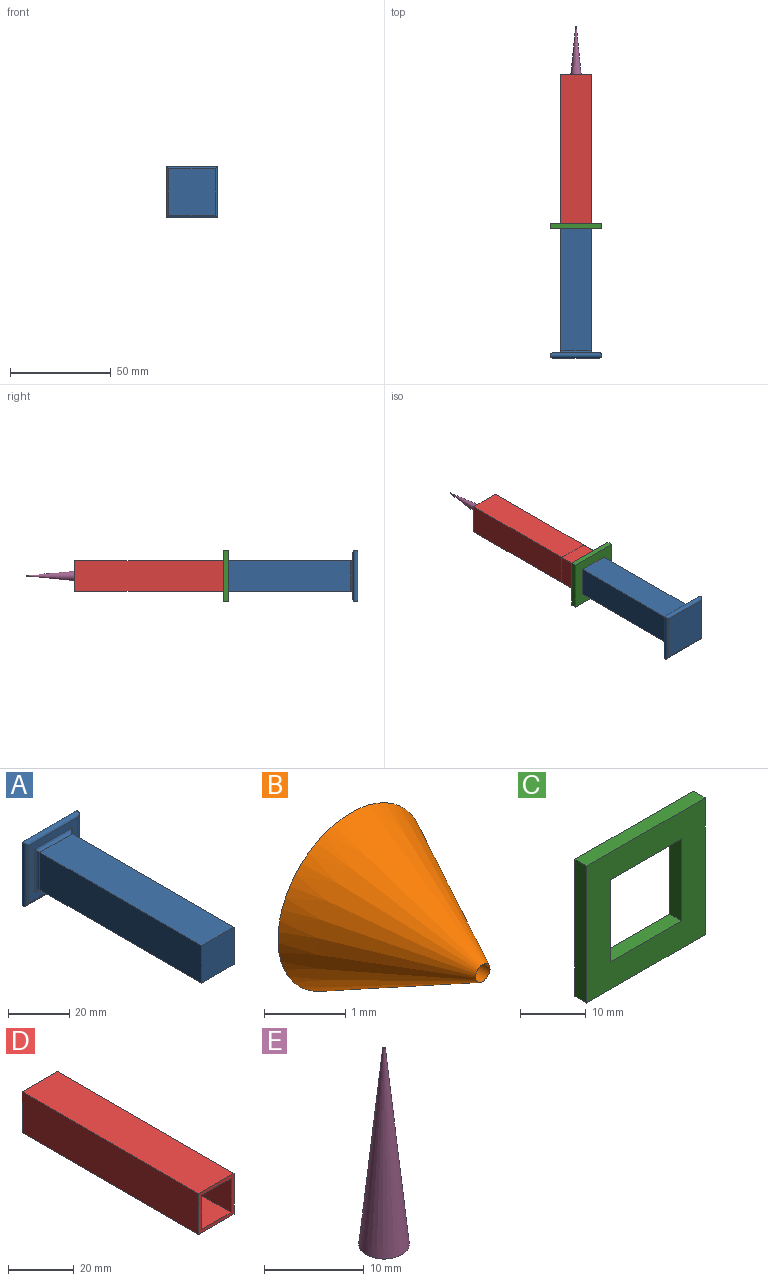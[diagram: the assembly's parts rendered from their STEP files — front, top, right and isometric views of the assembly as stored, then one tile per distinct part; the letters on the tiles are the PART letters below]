
ASSEMBLY  parts=5 mates=6
PART A: 15 faces, bbox 25.4x78.7x25.4 mm
  f0: plane 22.86x22.86mm, normal (0,-1,0), area 215.4mm2, adj f7,f8,f9,f10,f11,f12,f13,f14
  f1: plane 22.86x22.86mm, normal (0,1,0), area 522.6mm2, adj f11,f12,f13,f14
  f2: plane 74.93x14.99mm, normal (-1,0,0), area 1122.9mm2, adj f3,f5,f6,f7
  f3: plane 74.93x14.99mm, normal (0,0,-1), area 1122.9mm2, adj f2,f4,f6,f9
  f4: plane 74.93x14.99mm, normal (1,0,0), area 1122.9mm2, adj f3,f5,f6,f10
  f5: plane 74.93x14.99mm, normal (0,0,1), area 1122.9mm2, adj f2,f4,f6,f8
  f6: plane 14.99x14.99mm, normal (0,-1,0), area 224.6mm2, adj f2,f3,f4,f5
  f7: cylinder r=1.27mm len=17.53mm, axis (0,0,-1), area 31.7mm2, adj f0,f2,f8,f9
  f8: cylinder r=1.27mm len=17.53mm, axis (-1,0,0), area 31.7mm2, adj f0,f5,f7,f10
  f9: cylinder r=1.27mm len=17.53mm, axis (1,0,0), area 31.7mm2, adj f0,f3,f7,f10
  f10: cylinder r=1.27mm len=17.53mm, axis (0,0,1), area 31.7mm2, adj f0,f4,f8,f9
  f11: cylinder r=1.27mm len=25.41mm, axis (0,0,1), area 97.7mm2, adj f0,f1,f12,f13
  f12: cylinder r=1.27mm len=25.41mm, axis (1,0,0), area 97.7mm2, adj f0,f1,f11,f14
  f13: cylinder r=1.27mm len=25.41mm, axis (-1,0,0), area 97.7mm2, adj f0,f1,f11,f14
  f14: cylinder r=1.27mm len=25.41mm, axis (0,0,-1), area 97.7mm2, adj f0,f1,f12,f13
PART B: 3 faces, bbox 2.5x2.3x2.5 mm
  f0: plane 2.54x2.54mm, normal (0,1,0), area 5mm2, adj f1,f2
  f1: cone r=1.27mm half-angle=26.6deg, axis (0,1,0), area 11.2mm2, adj f0,f2
  f2: cylinder r=0.13mm len=2.29mm, axis (0,1,0), area 1.8mm2, adj f0,f1
PART C: 10 faces, bbox 25.4x2.5x25.4 mm
  f0: plane 25.4x2.54mm, normal (-1,0,0), area 64.5mm2, adj f1,f3,f4,f5
  f1: plane 25.4x2.54mm, normal (0,0,-1), area 64.5mm2, adj f0,f2,f4,f5
  f2: plane 25.4x2.54mm, normal (1,0,0), area 64.5mm2, adj f1,f3,f4,f5
  f3: plane 25.4x2.54mm, normal (0,0,1), area 64.5mm2, adj f0,f2,f4,f5
  f4: plane 25.4x25.4mm, normal (0,-1,0), area 412.9mm2, adj f0,f1,f2,f3,f6,f7,f8,f9
  f5: plane 25.4x25.4mm, normal (0,1,0), area 412.9mm2, adj f0,f1,f2,f3,f6,f7,f8,f9
  f6: plane 15.24x2.54mm, normal (1,0,0), area 38.7mm2, adj f4,f5,f7,f9
  f7: plane 15.24x2.54mm, normal (0,0,1), area 38.7mm2, adj f4,f5,f6,f8
  f8: plane 15.24x2.54mm, normal (-1,0,0), area 38.7mm2, adj f4,f5,f7,f9
  f9: plane 15.24x2.54mm, normal (0,0,-1), area 38.7mm2, adj f4,f5,f6,f8
PART D: 12 faces, bbox 15.2x76.2x15.2 mm
  f0: plane 76.2x15.24mm, normal (0,0,1), area 1161.3mm2, adj f1,f3,f4,f5
  f1: plane 76.2x15.24mm, normal (-1,0,0), area 1161.3mm2, adj f0,f2,f4,f5
  f2: plane 76.2x15.24mm, normal (0,0,-1), area 1161.3mm2, adj f1,f3,f4,f5
  f3: plane 76.2x15.24mm, normal (1,0,0), area 1161.3mm2, adj f0,f2,f4,f5
  f4: plane 15.24x15.24mm, normal (0,-1,0), area 71mm2, adj f0,f1,f2,f3,f6,f7,f8,f9
  f5: plane 15.24x15.24mm, normal (0,1,0), area 232.2mm2, adj f0,f1,f2,f3,f11
  f6: plane 73.66x12.7mm, normal (1,0,0), area 935.5mm2, adj f4,f7,f9,f10
  f7: plane 73.66x12.7mm, normal (0,0,1), area 935.5mm2, adj f4,f6,f8,f10
  f8: plane 73.66x12.7mm, normal (-1,0,0), area 935.5mm2, adj f4,f7,f9,f10
  f9: plane 73.66x12.7mm, normal (0,0,-1), area 935.5mm2, adj f4,f6,f8,f10
  f10: plane 12.7x12.7mm, normal (0,-1,0), area 161.2mm2, adj f6,f7,f8,f9,f11
  f11: cylinder r=0.13mm len=2.54mm, axis (0,1,0), area 2mm2, adj f5,f10
PART E: 3 faces, bbox 5.1x5.1x24.1 mm
  f0: plane 5.08x5.08mm, normal (0,0,-1), area 20.2mm2, adj f1,f2
  f1: cone r=2.54mm half-angle=5.7deg, axis (0,0,-1), area 203.2mm2, adj f0,f2
  f2: cylinder r=0.13mm len=24.13mm, axis (0,0,-1), area 19.3mm2, adj f0,f1
PLACE A rot(axis=(0.71,0,0.71),180deg) t=(-22.07,-49.11,36.07)mm
PLACE B t=(-22.07,88.68,36.07)mm
PLACE C t=(-22.07,17.56,36.07)mm
PLACE D t=(-22.07,93.76,36.07)mm
PLACE E rot(axis=(-1,0,0),90deg) t=(-19.11,91.03,33.53)mm
MATE revolute E.f1 <-> D.f11  axis (0,-1,0) through (-22.07,91.22,36.07)mm
MATE parallel A.f6 <-> D.f11  axis (0,1,0) through (-22.07,29.63,36.07)mm
MATE parallel A.f6 <-> D.f11  axis (0,1,0) through (-22.07,29.63,36.07)mm
MATE parallel C.f8 <-> D.f3  axis (-1,0,0) through (-14.45,16.29,36.07)mm
MATE parallel A.f6 <-> B.f1  axis (0,1,0) through (-22.07,29.63,36.07)mm
MATE parallel B.f1 <-> D.f11  axis (0,1,0) through (-22.07,88.68,36.07)mm
